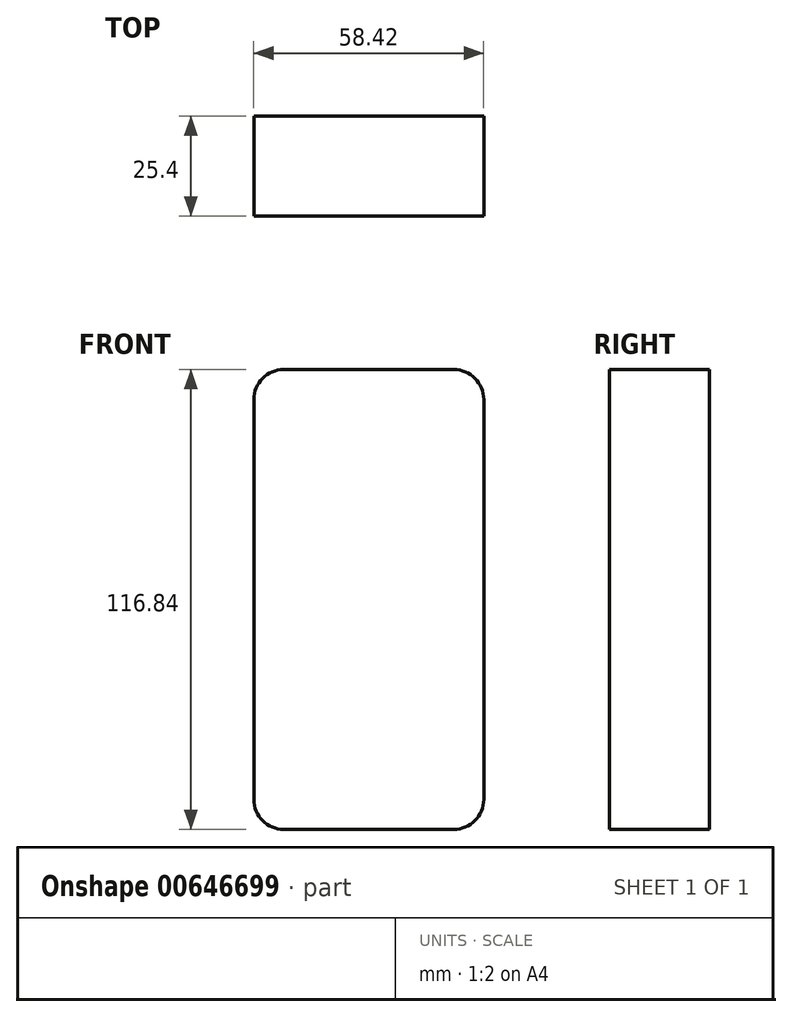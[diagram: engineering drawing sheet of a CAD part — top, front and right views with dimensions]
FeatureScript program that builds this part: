
annotation { "Feature Type Name" : "Feature", "Feature Type Description" : "" }
export const myFeature = defineFeature(function(context is Context, id is Id, definition is map)
    precondition{}
    {
        {
            var Q0;
            Q0=qCreatedBy(makeId("Front.planeOp"),FACE);
            var sketch = newSketch(context, id + "F0", { "sketchPlane" : qUnion([Q0])});
            skLineSegment(sketch, "E0.bottom", {"start": v(24.8, 68.34) * mm, "end": v(67.97, 68.34) * mm});
            skLineSegment(sketch, "E0.top", {"start": v(24.8, -48.5) * mm, "end": v(67.97, -48.5) * mm});
            skLineSegment(sketch, "E0.left", {"start": v(17.17, 60.72) * mm, "end": v(17.17, -40.88) * mm});
            skLineSegment(sketch, "E0.right", {"start": v(75.6, 60.72) * mm, "end": v(75.6, -40.88) * mm});
            skPoint(sketch, "E1.visualSharp", {"position": v(17.17, 68.34) * mm});
            skArc(sketch, "E1.filletArc", {"start": v(24.8, 68.34) * mm, "mid": v(19.4, 66.1) * mm, "end": v(17.17, 60.72) * mm});
            skPoint(sketch, "E2.visualSharp", {"position": v(75.6, 68.34) * mm});
            skArc(sketch, "E2.filletArc", {"start": v(75.6, 60.72) * mm, "mid": v(73.36, 66.1) * mm, "end": v(67.97, 68.34) * mm});
            skPoint(sketch, "E3.visualSharp", {"position": v(75.6, -48.5) * mm});
            skArc(sketch, "E3.filletArc", {"start": v(67.97, -48.5) * mm, "mid": v(73.36, -46.27) * mm, "end": v(75.6, -40.88) * mm});
            skPoint(sketch, "E4.visualSharp", {"position": v(17.17, -48.5) * mm});
            skArc(sketch, "E4.filletArc", {"start": v(17.17, -40.88) * mm, "mid": v(19.4, -46.27) * mm, "end": v(24.8, -48.5) * mm});
            skSolve(sketch);
        }
        {
            var Q0;
            Q0 = qSketchRegion(id + "F0", true);
            extrude(context, id + "F1", {"entities" : qUnion([Q0]), "depth" : 25.4 * mm, "offsetDistance" : 25.4 * mm});
        }
    });
